# Revit family: Maxlogic Блок интеграции с системой речевого оповещения
name_source: partatom
category: Fire Alarm Devices
units: mm (PartAtom-declared; Revit-internal decimal feet)

## family parameters
Cut with Voids When Loaded = No
Host = Face
Maintain Annotation Orientation = Yes
OmniClass Number = 23.85.30.21
OmniClass Title = Environmental Detection/Registration
Part Type = Normal
Room Calculation Point = No
Round Connector Dimension = Use Diameter
Shared = No

## types (1)
- Блок интеграции с системой речевого оповещения, базовая модель 19", 3U
    Cost = 0 $
    Default Elevation = 0 mm  [stored 0 ft]
    Description = Блок интеграции с системой речевого оповещения, базовая модель 19", 3U
    Manufacturer = Mavili Elektronik Ticaret A.Ş.
    Model = Maxlogic
    URL = https://www.mavili.com.tr
    Адрес №1 = Şerifali Mahallesi Kutup Sokak No:27/1-2-4 Ümraniye TR-34775 İSTANBUL
    Аккумулятор = 2 X (12В Пост. ток 7 Aм/ч. )
    Вторичный материал = Органическое стекло / плексиглас
    Гарантийный срок = Года
    Гарантийный срок запчастей = 2
    Гарантия срока службы = 2
    Главный Материал = Красный металлический
    Диапазон рабочего напряжения = 28 В Пост. ток
    Инструкция по установке = https://mavilielektronik.com
    Код продукта = ML-5020
    Монтажная поверхность = Rack
    Настройка адреса устройства = Модульная адресация
    Номер телефона = (+)90 216 466 45 05
    Номер факса = (+)90 216 466 45 10
    Номинальная высота = 133 мм
    Номинальная глубина = 209 мм
    Номинальная ширина = 483 мм
    Объявить модуль ввода = ML-5020.AI получает 4 адреса
    Программируемый модуль вывода тревоги / оповещения = ML-5020.PO получает 8 адресов
    Производительность кода = EN 54-16
    Пустая панель матрицы оповещения / тревоги = MLY-5001
    Рабочая Температура = (-10°C) - (+55°C)
    Рабочее напряжение (по умолчанию) = 28 В Пост. ток
    Резервное питание = 220 В Перем. ток
    Цвет = Черный

note: [stored X ft] marks values corroborated as IEEE doubles in the binary element streams (Revit-internal decimal feet)

## geometry (parser evidence)
native form markers: Sweep x2
no freeform markers — native parametric forms only
